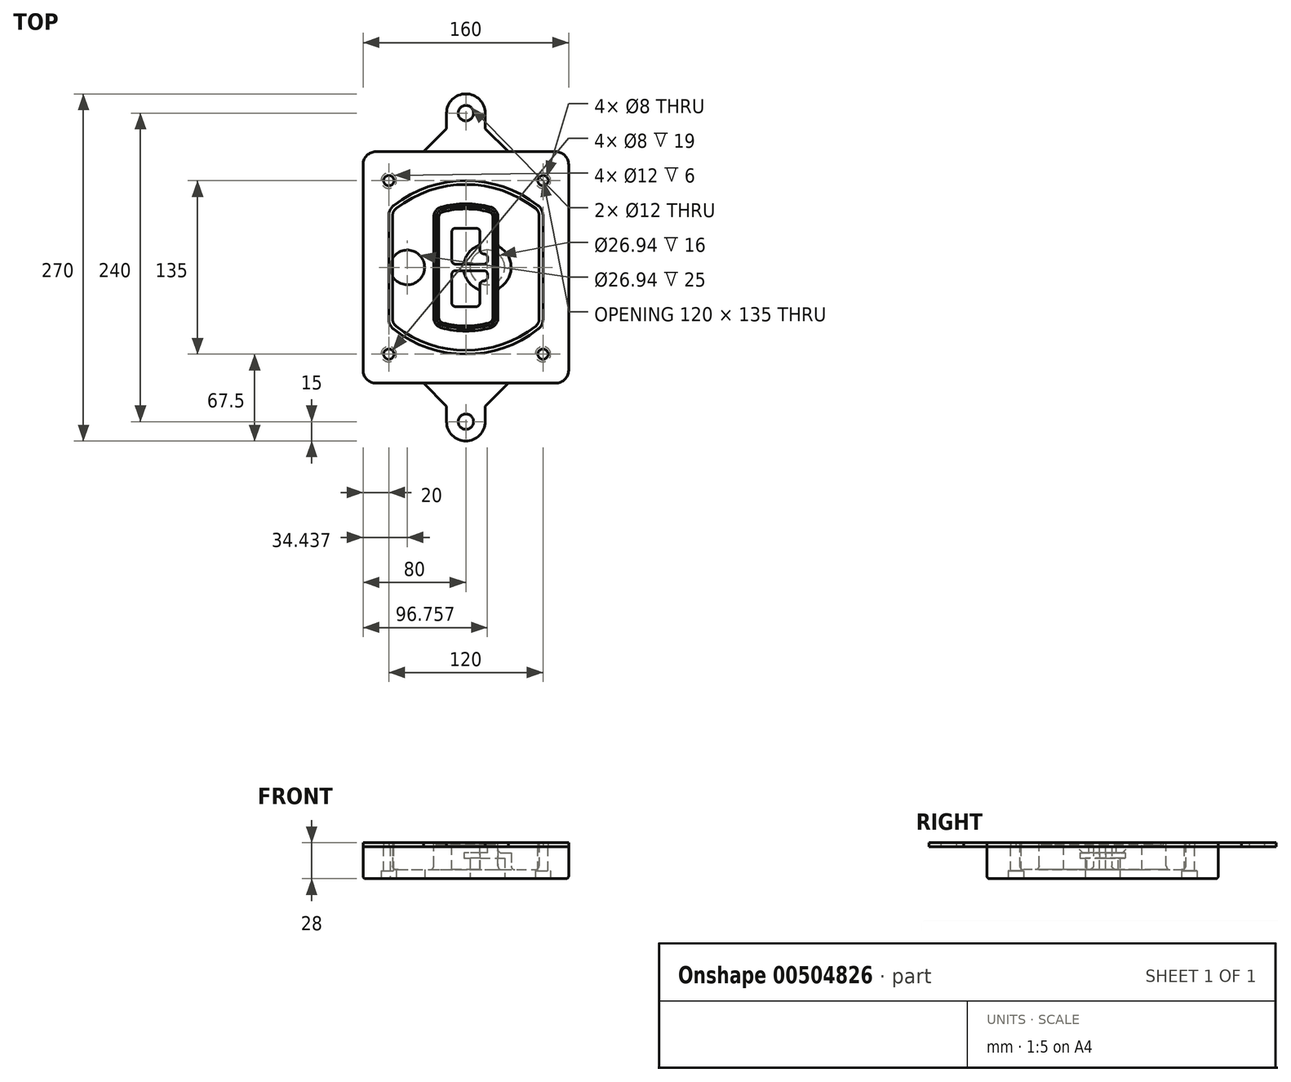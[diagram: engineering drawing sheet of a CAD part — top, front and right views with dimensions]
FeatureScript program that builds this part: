
annotation { "Feature Type Name" : "Feature", "Feature Type Description" : "" }
export const myFeature = defineFeature(function(context is Context, id is Id, definition is map)
    precondition{}
    {
        {
            var Q0;
            Q0=qCreatedBy(makeId("Top.planeOp"),FACE);
            var sketch = newSketch(context, id + "F0", { "sketchPlane" : qUnion([Q0])});
            skPoint(sketch, "E0.rect.middle", {"position": v(0, 0) * mm});
            skLineSegment(sketch, "E1.bottom", {"start": v(-70, -90) * mm, "end": v(70, -90) * mm});
            skLineSegment(sketch, "E1.top", {"start": v(-70, 90) * mm, "end": v(70, 90) * mm});
            skLineSegment(sketch, "E1.left", {"start": v(-80, -80) * mm, "end": v(-80, 80) * mm});
            skLineSegment(sketch, "E1.right", {"start": v(80, -80) * mm, "end": v(80, 80) * mm});
            skLineSegment(sketch, "E2", {"start": v(-80, 90) * mm, "end": v(80, -90) * mm, "construction": true});
            skLineSegment(sketch, "E3", {"start": v(80, 90) * mm, "end": v(-80, -90) * mm, "construction": true});
            skCircle(sketch, "E4", {"center": v(-60, 67.5) * mm, "radius": 4 * mm});
            skCircle(sketch, "E5", {"center": v(60, 67.5) * mm, "radius": 4 * mm});
            skCircle(sketch, "E6", {"center": v(60, -67.5) * mm, "radius": 4 * mm});
            skCircle(sketch, "E7", {"center": v(-60, -67.5) * mm, "radius": 4 * mm});
            skLineSegment(sketch, "E8", {"start": v(-60, 67.5) * mm, "end": v(60, 67.5) * mm, "construction": true});
            skLineSegment(sketch, "E9", {"start": v(60, 67.5) * mm, "end": v(60, -67.5) * mm, "construction": true});
            skLineSegment(sketch, "E10", {"start": v(60, -67.5) * mm, "end": v(-60, -67.5) * mm, "construction": true});
            skLineSegment(sketch, "E11", {"start": v(-60, -67.5) * mm, "end": v(-60, 67.5) * mm, "construction": true});
            skLineSegment(sketch, "E12", {"start": v(-60, 40.3) * mm, "end": v(-60, -40.3) * mm});
            skLineSegment(sketch, "E13", {"start": v(60, 40.3) * mm, "end": v(60, -40.3) * mm});
            skArc(sketch, "E14", {"start": v(56.15, 48.18) * mm, "mid": v(0, 67.5) * mm, "end": v(-56.15, 48.18) * mm});
            skArc(sketch, "E15", {"start": v(-56.15, -48.18) * mm, "mid": v(0, -67.5) * mm, "end": v(56.15, -48.18) * mm});
            skLineSegment(sketch, "E16", {"start": v(-60, 0) * mm, "end": v(60, 0) * mm, "construction": true});
            skPoint(sketch, "E17.visualSharp", {"position": v(-60, -45) * mm});
            skArc(sketch, "E17.filletArc", {"start": v(-60, -40.3) * mm, "mid": v(-58.99, -44.68) * mm, "end": v(-56.15, -48.18) * mm});
            skPoint(sketch, "E18.visualSharp", {"position": v(-60, 45) * mm});
            skArc(sketch, "E18.filletArc", {"start": v(-56.15, 48.18) * mm, "mid": v(-58.99, 44.68) * mm, "end": v(-60, 40.3) * mm});
            skPoint(sketch, "E19.visualSharp", {"position": v(60, 45) * mm});
            skArc(sketch, "E19.filletArc", {"start": v(60, 40.3) * mm, "mid": v(58.99, 44.68) * mm, "end": v(56.15, 48.18) * mm});
            skPoint(sketch, "E20.visualSharp", {"position": v(60, -45) * mm});
            skArc(sketch, "E20.filletArc", {"start": v(56.15, -48.18) * mm, "mid": v(58.99, -44.68) * mm, "end": v(60, -40.3) * mm});
            skPoint(sketch, "E21.visualSharp", {"position": v(-80, 90) * mm});
            skArc(sketch, "E21.filletArc", {"start": v(-70, 90) * mm, "mid": v(-77.07, 87.07) * mm, "end": v(-80, 80) * mm});
            skPoint(sketch, "E22.visualSharp", {"position": v(80, 90) * mm});
            skArc(sketch, "E22.filletArc", {"start": v(80, 80) * mm, "mid": v(77.07, 87.07) * mm, "end": v(70, 90) * mm});
            skPoint(sketch, "E23.visualSharp", {"position": v(80, -90) * mm});
            skArc(sketch, "E23.filletArc", {"start": v(70, -90) * mm, "mid": v(77.07, -87.07) * mm, "end": v(80, -80) * mm});
            skPoint(sketch, "E24.visualSharp", {"position": v(-80, -90) * mm});
            skArc(sketch, "E24.filletArc", {"start": v(-80, -80) * mm, "mid": v(-77.07, -87.07) * mm, "end": v(-70, -90) * mm});
            skArc(sketch, "E25.0", {"start": v(57, 40.3) * mm, "mid": v(56.3, 43.36) * mm, "end": v(54.3, 45.81) * mm});
            skLineSegment(sketch, "E25.1", {"start": v(57, 40.3) * mm, "end": v(57, -40.3) * mm});
            skArc(sketch, "E25.2", {"start": v(54.3, -45.81) * mm, "mid": v(56.3, -43.36) * mm, "end": v(57, -40.3) * mm});
            skArc(sketch, "E25.3", {"start": v(-54.3, -45.81) * mm, "mid": v(0, -64.5) * mm, "end": v(54.3, -45.81) * mm});
            skArc(sketch, "E25.4", {"start": v(-57, -40.3) * mm, "mid": v(-56.3, -43.36) * mm, "end": v(-54.3, -45.81) * mm});
            skArc(sketch, "E25.5", {"start": v(54.3, 45.81) * mm, "mid": v(0, 64.5) * mm, "end": v(-54.3, 45.81) * mm});
            skLineSegment(sketch, "E25.6", {"start": v(-57, 40.3) * mm, "end": v(-57, -40.3) * mm});
            skArc(sketch, "E25.7", {"start": v(-54.3, 45.81) * mm, "mid": v(-56.3, 43.36) * mm, "end": v(-57, 40.3) * mm});
            skArc(sketch, "E26.0", {"start": v(-58.62, 51.33) * mm, "mid": v(-62.58, 46.43) * mm, "end": v(-64, 40.3) * mm});
            skArc(sketch, "E26.1", {"start": v(58.62, 51.33) * mm, "mid": v(0, 71.5) * mm, "end": v(-58.62, 51.33) * mm});
            skArc(sketch, "E26.2", {"start": v(64, 40.3) * mm, "mid": v(62.58, 46.43) * mm, "end": v(58.62, 51.33) * mm});
            skLineSegment(sketch, "E26.3", {"start": v(64, 40.3) * mm, "end": v(64, -40.3) * mm});
            skArc(sketch, "E26.4", {"start": v(58.62, -51.33) * mm, "mid": v(62.58, -46.43) * mm, "end": v(64, -40.3) * mm});
            skLineSegment(sketch, "E26.5", {"start": v(-64, 40.3) * mm, "end": v(-64, -40.3) * mm});
            skArc(sketch, "E26.6", {"start": v(-58.62, -51.33) * mm, "mid": v(0, -71.5) * mm, "end": v(58.62, -51.33) * mm});
            skArc(sketch, "E26.7", {"start": v(-64, -40.3) * mm, "mid": v(-62.58, -46.43) * mm, "end": v(-58.62, -51.33) * mm});
            skSolve(sketch);
        }
        {
            var Q0;
            Q0=makeQuery(id+"F0.imprint","IMPRINT",FACE,{"disambiguationData":[TD([[makeQuery(id+"F0.imprint","IMPRINT",EDGE,{"derivedFrom":sQuery(id+"F0.wireOp",EDGE,"E1.bottom")}),1.0]])]});
            var Q1;
            Q1=makeQuery(id+"F0.imprint","IMPRINT",FACE,{"disambiguationData":[TD([[makeQuery(id+"F0.imprint","IMPRINT",EDGE,{"derivedFrom":sQuery(id+"F0.wireOp",EDGE,"E12")}),1.0]])]});
            var Q2;
            Q2=makeQuery(id+"F0.imprint","IMPRINT",FACE,{"disambiguationData":[TD([[makeQuery(id+"F0.imprint","IMPRINT",EDGE,{"derivedFrom":sQuery(id+"F0.wireOp",EDGE,"E25.0")}),1.0]])]});
            var Q3;
            Q3=makeQuery(id+"F0.imprint","IMPRINT",FACE,{"disambiguationData":[TD([[makeQuery(id+"F0.imprint","IMPRINT",EDGE,{"derivedFrom":sQuery(id+"F0.wireOp",EDGE,"E12")}),-1.0]])]});
            extrude(context, id + "F1", {"entities" : qUnion([Q0, Q1, Q2, Q3]), "oppositeDirection" : true, "depth" : 25 * mm});
        }
        {
            var Q0;
            Q0=makeQuery(id+"F0.imprint","IMPRINT",FACE,{"disambiguationData":[TD([[makeQuery(id+"F0.imprint","IMPRINT",EDGE,{"derivedFrom":sQuery(id+"F0.wireOp",EDGE,"E12")}),1.0]])]});
            extrude(context, id + "F2", {"entities" : qUnion([Q0]), "operationType" : NewBodyOperationType.ADD, "depth" : 3 * mm});
        }
        {
            var Q0;
            Q0=makeQuery(id+"F0.imprint","IMPRINT",FACE,{"disambiguationData":[TD([[makeQuery(id+"F0.imprint","IMPRINT",EDGE,{"derivedFrom":sQuery(id+"F0.wireOp",EDGE,"E25.0")}),1.0]])]});
            extrude(context, id + "F3", {"entities" : qUnion([Q0]), "operationType" : NewBodyOperationType.REMOVE, "oppositeDirection" : true, "depth" : 18 * mm});
        }
        {
            var Q0;
            Q0=makeQuery(id+"F2.opExtrude","CAP_FACE",FACE,{"disambiguationData":[OSD([sQuery(id+"F0.wireOp",EDGE,"E12"),sQuery(id+"F0.wireOp",EDGE,"E13"),sQuery(id+"F0.wireOp",EDGE,"E14"),sQuery(id+"F0.wireOp",EDGE,"E15"),sQuery(id+"F0.wireOp",EDGE,"E17.filletArc"),sQuery(id+"F0.wireOp",EDGE,"E18.filletArc"),sQuery(id+"F0.wireOp",EDGE,"E19.filletArc"),sQuery(id+"F0.wireOp",EDGE,"E20.filletArc"),sQuery(id+"F0.wireOp",EDGE,"E25.0"),sQuery(id+"F0.wireOp",EDGE,"E25.1"),sQuery(id+"F0.wireOp",EDGE,"E25.2"),sQuery(id+"F0.wireOp",EDGE,"E25.3"),sQuery(id+"F0.wireOp",EDGE,"E25.4"),sQuery(id+"F0.wireOp",EDGE,"E25.5"),sQuery(id+"F0.wireOp",EDGE,"E25.6"),sQuery(id+"F0.wireOp",EDGE,"E25.7")])],"isStart":false});
            var sketch = newSketch(context, id + "F4", { "sketchPlane" : qUnion([Q0])});
            skArc(sketch, "E27.0", {"start": v(-19.08, -46.97) * mm, "mid": v(0, -49.5) * mm, "end": v(19.08, -46.97) * mm});
            skArc(sketch, "E28.0", {"start": v(19.08, 46.97) * mm, "mid": v(0, 49.5) * mm, "end": v(-19.08, 46.97) * mm});
            skLineSegment(sketch, "E29", {"start": v(-25, 39.25) * mm, "end": v(-25, -39.25) * mm});
            skLineSegment(sketch, "E30", {"start": v(25, 39.25) * mm, "end": v(25, -39.25) * mm});
            skLineSegment(sketch, "E31", {"start": v(-25, 45.1) * mm, "end": v(25, 45.1) * mm, "construction": true});
            skLineSegment(sketch, "E32", {"start": v(-25, -45.1) * mm, "end": v(25, -45.1) * mm, "construction": true});
            skPoint(sketch, "E33.visualSharp", {"position": v(-25, 45.1) * mm});
            skArc(sketch, "E33.filletArc", {"start": v(-19.08, 46.97) * mm, "mid": v(-23.35, 44.11) * mm, "end": v(-25, 39.25) * mm});
            skPoint(sketch, "E34.visualSharp", {"position": v(25, 45.1) * mm});
            skArc(sketch, "E34.filletArc", {"start": v(25, 39.25) * mm, "mid": v(23.35, 44.11) * mm, "end": v(19.08, 46.97) * mm});
            skPoint(sketch, "E35.visualSharp", {"position": v(25, -45.1) * mm});
            skArc(sketch, "E35.filletArc", {"start": v(19.08, -46.97) * mm, "mid": v(23.35, -44.11) * mm, "end": v(25, -39.25) * mm});
            skPoint(sketch, "E36.visualSharp", {"position": v(-25, -45.1) * mm});
            skArc(sketch, "E36.filletArc", {"start": v(-25, -39.25) * mm, "mid": v(-23.35, -44.11) * mm, "end": v(-19.08, -46.97) * mm});
            skArc(sketch, "E37.0", {"start": v(54.3, 45.81) * mm, "mid": v(0, 64.5) * mm, "end": v(-54.3, 45.81) * mm});
            skArc(sketch, "E37.1", {"start": v(-54.3, 45.81) * mm, "mid": v(-56.3, 43.36) * mm, "end": v(-57, 40.3) * mm});
            skLineSegment(sketch, "E37.2", {"start": v(-57, 40.3) * mm, "end": v(-57, -40.3) * mm});
            skArc(sketch, "E37.3", {"start": v(-57, -40.3) * mm, "mid": v(-56.3, -43.36) * mm, "end": v(-54.3, -45.81) * mm});
            skArc(sketch, "E37.4", {"start": v(-54.3, -45.81) * mm, "mid": v(0, -64.5) * mm, "end": v(54.3, -45.81) * mm});
            skArc(sketch, "E37.5", {"start": v(54.3, -45.81) * mm, "mid": v(56.3, -43.36) * mm, "end": v(57, -40.3) * mm});
            skLineSegment(sketch, "E37.6", {"start": v(57, 40.3) * mm, "end": v(57, -40.3) * mm});
            skArc(sketch, "E37.7", {"start": v(57, 40.3) * mm, "mid": v(56.3, 43.36) * mm, "end": v(54.3, 45.81) * mm});
            skLineSegment(sketch, "E38.0", {"start": v(23, 39.25) * mm, "end": v(23, -39.25) * mm});
            skArc(sketch, "E38.1", {"start": v(18.56, -45.04) * mm, "mid": v(21.76, -42.9) * mm, "end": v(23, -39.25) * mm});
            skArc(sketch, "E38.2", {"start": v(-18.56, -45.04) * mm, "mid": v(0, -47.5) * mm, "end": v(18.56, -45.04) * mm});
            skArc(sketch, "E38.3", {"start": v(-23, -39.25) * mm, "mid": v(-21.76, -42.9) * mm, "end": v(-18.56, -45.04) * mm});
            skLineSegment(sketch, "E38.4", {"start": v(-23, 39.25) * mm, "end": v(-23, -39.25) * mm});
            skArc(sketch, "E38.5", {"start": v(23, 39.25) * mm, "mid": v(21.76, 42.9) * mm, "end": v(18.56, 45.04) * mm});
            skArc(sketch, "E38.6", {"start": v(-18.56, 45.04) * mm, "mid": v(-21.76, 42.9) * mm, "end": v(-23, 39.25) * mm});
            skArc(sketch, "E38.7", {"start": v(18.56, 45.04) * mm, "mid": v(0, 47.5) * mm, "end": v(-18.56, 45.04) * mm});
            skArc(sketch, "E39.0", {"start": v(21, 39.25) * mm, "mid": v(20.18, 41.68) * mm, "end": v(18.04, 43.1) * mm});
            skLineSegment(sketch, "E39.1", {"start": v(21, 39.25) * mm, "end": v(21, -39.25) * mm});
            skArc(sketch, "E39.2", {"start": v(18.04, -43.1) * mm, "mid": v(20.18, -41.68) * mm, "end": v(21, -39.25) * mm});
            skArc(sketch, "E39.3", {"start": v(-18.04, -43.1) * mm, "mid": v(0, -45.5) * mm, "end": v(18.04, -43.1) * mm});
            skArc(sketch, "E39.4", {"start": v(-21, -39.25) * mm, "mid": v(-20.18, -41.68) * mm, "end": v(-18.04, -43.1) * mm});
            skArc(sketch, "E39.5", {"start": v(18.04, 43.1) * mm, "mid": v(0, 45.5) * mm, "end": v(-18.04, 43.1) * mm});
            skLineSegment(sketch, "E39.6", {"start": v(-21, 39.25) * mm, "end": v(-21, -39.25) * mm});
            skArc(sketch, "E39.7", {"start": v(-18.04, 43.1) * mm, "mid": v(-20.18, 41.68) * mm, "end": v(-21, 39.25) * mm});
            skLineSegment(sketch, "E40", {"start": v(-25, 0) * mm, "end": v(25, 0) * mm, "construction": true});
            skLineSegment(sketch, "E41", {"start": v(-11, 5.5) * mm, "end": v(-11, 27.5) * mm});
            skLineSegment(sketch, "E42", {"start": v(-8, 30.5) * mm, "end": v(8, 30.5) * mm});
            skLineSegment(sketch, "E43", {"start": v(11, 27.5) * mm, "end": v(11, 13.5) * mm});
            skLineSegment(sketch, "E44", {"start": v(14, 10.5) * mm, "end": v(14, 10.5) * mm});
            skLineSegment(sketch, "E45", {"start": v(17, 7.5) * mm, "end": v(17, 5.5) * mm});
            skLineSegment(sketch, "E46", {"start": v(14, 2.5) * mm, "end": v(-8, 2.5) * mm});
            skPoint(sketch, "E47.visualSharp", {"position": v(-11, 30.5) * mm});
            skArc(sketch, "E47.filletArc", {"start": v(-8, 30.5) * mm, "mid": v(-10.12, 29.62) * mm, "end": v(-11, 27.5) * mm});
            skPoint(sketch, "E48.visualSharp", {"position": v(11, 30.5) * mm});
            skArc(sketch, "E48.filletArc", {"start": v(11, 27.5) * mm, "mid": v(10.12, 29.62) * mm, "end": v(8, 30.5) * mm});
            skPoint(sketch, "E49.visualSharp", {"position": v(11, 10.5) * mm});
            skArc(sketch, "E49.filletArc", {"start": v(11, 13.5) * mm, "mid": v(11.88, 11.38) * mm, "end": v(14, 10.5) * mm});
            skPoint(sketch, "E50.visualSharp", {"position": v(17, 10.5) * mm});
            skArc(sketch, "E50.filletArc", {"start": v(17, 7.5) * mm, "mid": v(16.12, 9.62) * mm, "end": v(14, 10.5) * mm});
            skPoint(sketch, "E51.visualSharp", {"position": v(17, 2.5) * mm});
            skArc(sketch, "E51.filletArc", {"start": v(14, 2.5) * mm, "mid": v(16.12, 3.38) * mm, "end": v(17, 5.5) * mm});
            skPoint(sketch, "E52.visualSharp", {"position": v(-11, 2.5) * mm});
            skArc(sketch, "E52.filletArc", {"start": v(-11, 5.5) * mm, "mid": v(-10.12, 3.38) * mm, "end": v(-8, 2.5) * mm});
            skLineSegment(sketch, "E53.0.MirrorCS", {"start": v(14, -2.5) * mm, "end": v(-8, -2.5) * mm});
            skArc(sketch, "E54.0.MirrorCS", {"start": v(-11, -5.5) * mm, "mid": v(-10.12, -3.38) * mm, "end": v(-8, -2.5) * mm});
            skLineSegment(sketch, "E55.0.MirrorCS", {"start": v(-11, -5.5) * mm, "end": v(-11, -27.5) * mm});
            skArc(sketch, "E56.0.MirrorCS", {"start": v(-8, -30.5) * mm, "mid": v(-10.12, -29.62) * mm, "end": v(-11, -27.5) * mm});
            skLineSegment(sketch, "E57.0.MirrorCS", {"start": v(-8, -30.5) * mm, "end": v(8, -30.5) * mm});
            skArc(sketch, "E58.0.MirrorCS", {"start": v(11, -27.5) * mm, "mid": v(10.12, -29.62) * mm, "end": v(8, -30.5) * mm});
            skLineSegment(sketch, "E59.0.MirrorCS", {"start": v(11, -27.5) * mm, "end": v(11, -13.5) * mm});
            skArc(sketch, "E60.0.MirrorCS", {"start": v(11, -13.5) * mm, "mid": v(11.88, -11.38) * mm, "end": v(14, -10.5) * mm});
            skArc(sketch, "E61.0.MirrorCS", {"start": v(17, -7.5) * mm, "mid": v(16.12, -9.62) * mm, "end": v(14, -10.5) * mm});
            skLineSegment(sketch, "E62.0.MirrorCS", {"start": v(17, -7.5) * mm, "end": v(17, -5.5) * mm});
            skArc(sketch, "E63.0.MirrorCS", {"start": v(14, -2.5) * mm, "mid": v(16.12, -3.38) * mm, "end": v(17, -5.5) * mm});
            skSolve(sketch);
        }
        {
            var Q0;
            Q0=makeQuery(id+"F4.imprint","IMPRINT",FACE,{"disambiguationData":[TD([[makeQuery(id+"F4.imprint","IMPRINT",EDGE,{"derivedFrom":sQuery(id+"F4.wireOp",EDGE,"E27.0")}),1.0]])]});
            var Q1;
            Q1=makeQuery(id+"F4.imprint","IMPRINT",FACE,{"disambiguationData":[TD([[makeQuery(id+"F4.imprint","IMPRINT",EDGE,{"derivedFrom":sQuery(id+"F4.wireOp",EDGE,"E38.0")}),-1.0]])]});
            var Q2;
            Q2=makeQuery(id+"F4.imprint","IMPRINT",FACE,{"disambiguationData":[TD([[makeQuery(id+"F4.imprint","IMPRINT",EDGE,{"derivedFrom":sQuery(id+"F4.wireOp",EDGE,"E39.0")}),1.0]])]});
            extrude(context, id + "F5", {"entities" : qUnion([Q0, Q1, Q2]), "operationType" : NewBodyOperationType.ADD, "endBound" : BoundingType.UP_TO_NEXT, "oppositeDirection" : true, "depth" : 25 * mm});
        }
        {
            var Q0;
            Q0=makeQuery(id+"F4.imprint","IMPRINT",FACE,{"disambiguationData":[TD([[makeQuery(id+"F4.imprint","IMPRINT",EDGE,{"derivedFrom":sQuery(id+"F4.wireOp",EDGE,"E38.0")}),-1.0]])]});
            extrude(context, id + "F6", {"entities" : qUnion([Q0]), "operationType" : NewBodyOperationType.REMOVE, "oppositeDirection" : true, "depth" : 2 * mm});
        }
        {
            var Q0;
            Q0=makeQuery(id+"F1.opExtrude","CAP_FACE",FACE,{"disambiguationData":[OSD([sQuery(id+"F0.wireOp",EDGE,"E1.bottom"),sQuery(id+"F0.wireOp",EDGE,"E1.top"),sQuery(id+"F0.wireOp",EDGE,"E1.left"),sQuery(id+"F0.wireOp",EDGE,"E1.right"),sQuery(id+"F0.wireOp",EDGE,"E4"),sQuery(id+"F0.wireOp",EDGE,"E5"),sQuery(id+"F0.wireOp",EDGE,"E6"),sQuery(id+"F0.wireOp",EDGE,"E7"),sQuery(id+"F0.wireOp",EDGE,"E21.filletArc"),sQuery(id+"F0.wireOp",EDGE,"E22.filletArc"),sQuery(id+"F0.wireOp",EDGE,"E23.filletArc"),sQuery(id+"F0.wireOp",EDGE,"E24.filletArc")])],"isStart":false});
            var sketch = newSketch(context, id + "F7", { "sketchPlane" : qUnion([Q0])});
            skCircle(sketch, "E64", {"center": v(16.76, 0) * mm, "radius": 13.47 * mm});
            skCircle(sketch, "E65", {"center": v(-45.56, 0) * mm, "radius": 13.47 * mm});
            skLineSegment(sketch, "E66", {"start": v(80, 0) * mm, "end": v(-80, 0) * mm});
            skCircle(sketch, "E67", {"center": v(16.76, 0) * mm, "radius": 18.47 * mm});
            skCircle(sketch, "E68", {"center": v(60, -67.5) * mm, "radius": 6 * mm});
            skCircle(sketch, "E69", {"center": v(-60, -67.5) * mm, "radius": 6 * mm});
            skCircle(sketch, "E70", {"center": v(-60, 67.5) * mm, "radius": 6 * mm});
            skCircle(sketch, "E71", {"center": v(60, 67.5) * mm, "radius": 6 * mm});
            skSolve(sketch);
        }
        {
            var Q0;
            {var subQ1=sQuery(id+"F7.wireOp",EDGE,"E66");var subQ4=sQuery(id+"F7.wireOp",EDGE,"E64");var subQ6=makeQuery(id+"F7.imprint","INTERSECT",VERTEX,{"disambiguationData":[OD(0.0)],"derivedFrom":[subQ4,subQ1]});Q0=makeQuery(id+"F7.imprint","IMPRINT",FACE,{"disambiguationData":[TD([[makeQuery(id+"F7.imprint","IMPRINT",EDGE,{"disambiguationData":[TD([[subQ6,-1.0]])],"derivedFrom":subQ4}),-1.0]])]});}
            var Q1;
            {var subQ0=sQuery(id+"F7.wireOp",EDGE,"E66");var subQ1=sQuery(id+"F7.wireOp",EDGE,"E64");var subQ3=makeQuery(id+"F7.imprint","INTERSECT",VERTEX,{"disambiguationData":[OD(0.0)],"derivedFrom":[subQ1,subQ0]});Q1=makeQuery(id+"F7.imprint","IMPRINT",FACE,{"disambiguationData":[TD([[makeQuery(id+"F7.imprint","IMPRINT",EDGE,{"disambiguationData":[TD([[subQ3,-1.0]])],"derivedFrom":subQ1}),1.0]])]});}
            var Q2;
            {var subQ0=sQuery(id+"F7.wireOp",EDGE,"E66");var subQ1=sQuery(id+"F7.wireOp",EDGE,"E64");var subQ3=makeQuery(id+"F7.imprint","INTERSECT",VERTEX,{"disambiguationData":[OD(0.0)],"derivedFrom":[subQ1,subQ0]});Q2=makeQuery(id+"F7.imprint","IMPRINT",FACE,{"disambiguationData":[TD([[makeQuery(id+"F7.imprint","IMPRINT",EDGE,{"disambiguationData":[TD([[subQ3,1.0]])],"derivedFrom":subQ1}),1.0]])]});}
            var Q3;
            {var subQ1=sQuery(id+"F7.wireOp",EDGE,"E66");var subQ4=sQuery(id+"F7.wireOp",EDGE,"E64");var subQ6=makeQuery(id+"F7.imprint","INTERSECT",VERTEX,{"disambiguationData":[OD(0.0)],"derivedFrom":[subQ4,subQ1]});Q3=makeQuery(id+"F7.imprint","IMPRINT",FACE,{"disambiguationData":[TD([[makeQuery(id+"F7.imprint","IMPRINT",EDGE,{"disambiguationData":[TD([[subQ6,1.0]])],"derivedFrom":subQ4}),-1.0]])]});}
            extrude(context, id + "F8", {"entities" : qUnion([Q0, Q1, Q2, Q3]), "operationType" : NewBodyOperationType.ADD, "oppositeDirection" : true, "depth" : 20 * mm});
        }
        {
            var Q0;
            {var subQ0=sQuery(id+"F7.wireOp",EDGE,"E66");var subQ1=sQuery(id+"F7.wireOp",EDGE,"E64");var subQ3=makeQuery(id+"F7.imprint","INTERSECT",VERTEX,{"disambiguationData":[OD(0.0)],"derivedFrom":[subQ1,subQ0]});Q0=makeQuery(id+"F7.imprint","IMPRINT",FACE,{"disambiguationData":[TD([[makeQuery(id+"F7.imprint","IMPRINT",EDGE,{"disambiguationData":[TD([[subQ3,-1.0]])],"derivedFrom":subQ1}),1.0]])]});}
            var Q1;
            {var subQ0=sQuery(id+"F7.wireOp",EDGE,"E66");var subQ1=sQuery(id+"F7.wireOp",EDGE,"E64");var subQ3=makeQuery(id+"F7.imprint","INTERSECT",VERTEX,{"disambiguationData":[OD(0.0)],"derivedFrom":[subQ1,subQ0]});Q1=makeQuery(id+"F7.imprint","IMPRINT",FACE,{"disambiguationData":[TD([[makeQuery(id+"F7.imprint","IMPRINT",EDGE,{"disambiguationData":[TD([[subQ3,1.0]])],"derivedFrom":subQ1}),1.0]])]});}
            extrude(context, id + "F9", {"entities" : qUnion([Q0, Q1]), "operationType" : NewBodyOperationType.REMOVE, "oppositeDirection" : true, "depth" : 16 * mm});
        }
        {
            var Q0;
            {var subQ0=sQuery(id+"F7.wireOp",EDGE,"E66");var subQ1=sQuery(id+"F7.wireOp",EDGE,"E65");var subQ3=makeQuery(id+"F7.imprint","INTERSECT",VERTEX,{"disambiguationData":[OD(0.0)],"derivedFrom":[subQ1,subQ0]});Q0=makeQuery(id+"F7.imprint","IMPRINT",FACE,{"disambiguationData":[TD([[makeQuery(id+"F7.imprint","IMPRINT",EDGE,{"disambiguationData":[TD([[subQ3,-1.0]])],"derivedFrom":subQ1}),1.0]])]});}
            var Q1;
            {var subQ0=sQuery(id+"F7.wireOp",EDGE,"E66");var subQ1=sQuery(id+"F7.wireOp",EDGE,"E65");var subQ3=makeQuery(id+"F7.imprint","INTERSECT",VERTEX,{"disambiguationData":[OD(0.0)],"derivedFrom":[subQ1,subQ0]});Q1=makeQuery(id+"F7.imprint","IMPRINT",FACE,{"disambiguationData":[TD([[makeQuery(id+"F7.imprint","IMPRINT",EDGE,{"disambiguationData":[TD([[subQ3,1.0]])],"derivedFrom":subQ1}),1.0]])]});}
            extrude(context, id + "F10", {"entities" : qUnion([Q0, Q1]), "operationType" : NewBodyOperationType.REMOVE, "oppositeDirection" : true, "depth" : 25 * mm});
        }
        {
            var Q0;
            Q0=makeQuery(id+"F7.imprint","IMPRINT",FACE,{"disambiguationData":[TD([[makeQuery(id+"F7.imprint","IMPRINT",EDGE,{"derivedFrom":sQuery(id+"F7.wireOp",EDGE,"E68")}),1.0]])]});
            var Q1;
            Q1=makeQuery(id+"F7.imprint","IMPRINT",FACE,{"disambiguationData":[TD([[makeQuery(id+"F7.imprint","IMPRINT",EDGE,{"derivedFrom":makeQuery(id+"F1.opExtrude","CAP_EDGE",EDGE,{"disambiguationData":[OSD([sQuery(id+"F0.wireOp",EDGE,"E5")])],"isStart":false})}),-1.0]])]});
            var Q2;
            Q2=makeQuery(id+"F7.imprint","IMPRINT",FACE,{"disambiguationData":[TD([[makeQuery(id+"F7.imprint","IMPRINT",EDGE,{"derivedFrom":sQuery(id+"F7.wireOp",EDGE,"E69")}),1.0]])]});
            var Q3;
            Q3=makeQuery(id+"F7.imprint","IMPRINT",FACE,{"disambiguationData":[TD([[makeQuery(id+"F7.imprint","IMPRINT",EDGE,{"derivedFrom":makeQuery(id+"F1.opExtrude","CAP_EDGE",EDGE,{"disambiguationData":[OSD([sQuery(id+"F0.wireOp",EDGE,"E4")])],"isStart":false})}),-1.0]])]});
            var Q4;
            Q4=makeQuery(id+"F7.imprint","IMPRINT",FACE,{"disambiguationData":[TD([[makeQuery(id+"F7.imprint","IMPRINT",EDGE,{"derivedFrom":sQuery(id+"F7.wireOp",EDGE,"E70")}),1.0]])]});
            var Q5;
            Q5=makeQuery(id+"F7.imprint","IMPRINT",FACE,{"disambiguationData":[TD([[makeQuery(id+"F7.imprint","IMPRINT",EDGE,{"derivedFrom":makeQuery(id+"F1.opExtrude","CAP_EDGE",EDGE,{"disambiguationData":[OSD([sQuery(id+"F0.wireOp",EDGE,"E7")])],"isStart":false})}),-1.0]])]});
            var Q6;
            Q6=makeQuery(id+"F7.imprint","IMPRINT",FACE,{"disambiguationData":[TD([[makeQuery(id+"F7.imprint","IMPRINT",EDGE,{"derivedFrom":sQuery(id+"F7.wireOp",EDGE,"E71")}),1.0]])]});
            var Q7;
            Q7=makeQuery(id+"F7.imprint","IMPRINT",FACE,{"disambiguationData":[TD([[makeQuery(id+"F7.imprint","IMPRINT",EDGE,{"derivedFrom":makeQuery(id+"F1.opExtrude","CAP_EDGE",EDGE,{"disambiguationData":[OSD([sQuery(id+"F0.wireOp",EDGE,"E6")])],"isStart":false})}),-1.0]])]});
            extrude(context, id + "F11", {"entities" : qUnion([Q0, Q1, Q2, Q3, Q4, Q5, Q6, Q7]), "operationType" : NewBodyOperationType.REMOVE, "oppositeDirection" : true, "depth" : 6 * mm});
        }
        {
            var Q0;
            Q0=makeQuery(id+"F9.boolean.opBoolean","COPY",FACE,{"derivedFrom":makeQuery(id+"F9.opExtrude","CAP_FACE",FACE,{"disambiguationData":[OSD([sQuery(id+"F7.wireOp",EDGE,"E64")])],"isStart":false})});
            var sketch = newSketch(context, id + "F12", { "sketchPlane" : qUnion([Q0])});
            skArc(sketch, "E72.0", {"start": v(11, 17.55) * mm, "mid": v(2.57, 11.82) * mm, "end": v(-1.54, 2.5) * mm});
            skArc(sketch, "E72.1", {"start": v(-1.54, -2.5) * mm, "mid": v(2.57, -11.82) * mm, "end": v(11, -17.55) * mm});
            skLineSegment(sketch, "E73", {"start": v(-1.54, -2.5) * mm, "end": v(14, -2.5) * mm});
            skLineSegment(sketch, "E74.0", {"start": v(14, 2.5) * mm, "end": v(-1.54, 2.5) * mm});
            skArc(sketch, "E74.1", {"start": v(14, 2.5) * mm, "mid": v(16.12, 3.38) * mm, "end": v(17, 5.5) * mm});
            skLineSegment(sketch, "E74.2", {"start": v(17, 7.5) * mm, "end": v(17, 5.5) * mm});
            skArc(sketch, "E74.3", {"start": v(17, 7.5) * mm, "mid": v(16.12, 9.62) * mm, "end": v(14, 10.5) * mm});
            skArc(sketch, "E74.4", {"start": v(11, 13.5) * mm, "mid": v(11.88, 11.38) * mm, "end": v(14, 10.5) * mm});
            skLineSegment(sketch, "E74.5", {"start": v(11, 17.55) * mm, "end": v(11, 13.5) * mm});
            skLineSegment(sketch, "E74.7", {"start": v(14, -2.5) * mm, "end": v(-1.54, -2.5) * mm});
            skArc(sketch, "E74.8", {"start": v(14, -2.5) * mm, "mid": v(16.12, -3.38) * mm, "end": v(17, -5.5) * mm});
            skLineSegment(sketch, "E74.9", {"start": v(17, -7.5) * mm, "end": v(17, -5.5) * mm});
            skArc(sketch, "E74.10", {"start": v(17, -7.5) * mm, "mid": v(16.12, -9.62) * mm, "end": v(14, -10.5) * mm});
            skArc(sketch, "E74.11", {"start": v(11, -13.5) * mm, "mid": v(11.88, -11.38) * mm, "end": v(14, -10.5) * mm});
            skLineSegment(sketch, "E74.12", {"start": v(11, -17.55) * mm, "end": v(11, -13.5) * mm});
            skPoint(sketch, "E75.orphan", {"position": v(11, -27.5) * mm});
            skPoint(sketch, "E76.orphan", {"position": v(-8, -2.5) * mm});
            skPoint(sketch, "E77.orphan", {"position": v(-8, 2.5) * mm});
            skPoint(sketch, "E78.orphan", {"position": v(11, 27.5) * mm});
            skSolve(sketch);
        }
        {
            var Q0;
            {var subQ7=sQuery(id+"F12.wireOp",EDGE,"E72.0");var subQ14=sQuery(id+"F12.wireOp",EDGE,"E72.1");var subQ16=sQuery(id+"F12.wireOp",EDGE,"E74.1");var subQ18=sQuery(id+"F12.wireOp",EDGE,"E74.8");Q0=qUnion([makeQuery(id+"F12.imprint","IMPRINT",FACE,{"disambiguationData":[TD([[makeQuery(id+"F12.imprint","IMPRINT",EDGE,{"derivedFrom":subQ7}),1.0]])]}),makeQuery(id+"F12.imprint","IMPRINT",FACE,{"disambiguationData":[TD([[makeQuery(id+"F12.imprint","IMPRINT",EDGE,{"derivedFrom":subQ14}),1.0]])]}),makeQuery(id+"F12.imprint","IMPRINT",FACE,{"disambiguationData":[TD([[makeQuery(id+"F12.imprint","IMPRINT",EDGE,{"derivedFrom":subQ16}),1.0]])]}),makeQuery(id+"F12.imprint","IMPRINT",FACE,{"disambiguationData":[TD([[makeQuery(id+"F12.imprint","IMPRINT",EDGE,{"derivedFrom":subQ18}),-1.0]])]})]);}
            var Q1;
            Q1=makeQuery(id+"F5.boolean.opBoolean","SPLIT",FACE,{"disambiguationData":[TD([makeQuery(id+"F5.opExtrude","SWEPT_FACE",FACE,{"disambiguationData":[OSD([sQuery(id+"F4.wireOp",EDGE,"E41")])]})])],"derivedFrom":makeQuery(id+"F3.boolean.opBoolean","COPY",FACE,{"derivedFrom":makeQuery(id+"F3.opExtrude","CAP_FACE",FACE,{"disambiguationData":[OSD([sQuery(id+"F0.wireOp",EDGE,"E25.0"),sQuery(id+"F0.wireOp",EDGE,"E25.1"),sQuery(id+"F0.wireOp",EDGE,"E25.2"),sQuery(id+"F0.wireOp",EDGE,"E25.3"),sQuery(id+"F0.wireOp",EDGE,"E25.4"),sQuery(id+"F0.wireOp",EDGE,"E25.5"),sQuery(id+"F0.wireOp",EDGE,"E25.6"),sQuery(id+"F0.wireOp",EDGE,"E25.7")])],"isStart":false})})});
            extrude(context, id + "F13", {"entities" : qUnion([Q0]), "operationType" : NewBodyOperationType.REMOVE, "endBound" : BoundingType.UP_TO_SURFACE, "endBoundEntityFace" : qUnion([Q1]), "depth" : 25 * mm});
        }
        {
            var Q0;
            Q0=makeQuery(id+"F3.boolean.opBoolean","COPY",EDGE,{"derivedFrom":makeQuery(id+"F3.opExtrude","CAP_EDGE",EDGE,{"disambiguationData":[OSD([sQuery(id+"F0.wireOp",EDGE,"E25.6")])],"isStart":false})});
            var Q1;
            Q1=makeQuery(id+"F8.boolean.opBoolean","INTERSECT",EDGE,{"derivedFrom":[makeQuery(id+"F5.opExtrude","SWEPT_FACE",FACE,{"disambiguationData":[OSD([sQuery(id+"F4.wireOp",EDGE,"E30")])]}),makeQuery(id+"F8.opExtrude","CAP_FACE",FACE,{"disambiguationData":[OSD([sQuery(id+"F7.wireOp",EDGE,"E67")])],"isStart":false})]});
            var Q2;
            Q2=makeQuery(id+"F8.boolean.opBoolean","INTERSECT",EDGE,{"disambiguationData":[OD(1.0)],"derivedFrom":[makeQuery(id+"F5.opExtrude","SWEPT_FACE",FACE,{"disambiguationData":[OSD([sQuery(id+"F4.wireOp",EDGE,"E30")])]}),makeQuery(id+"F8.opExtrude","SWEPT_FACE",FACE,{"disambiguationData":[OSD([sQuery(id+"F7.wireOp",EDGE,"E67")])]})]});
            var Q3;
            {var subQ0=sQuery(id+"F4.wireOp",EDGE,"E30");Q3=makeQuery(id+"F8.boolean.opBoolean","SPLIT",EDGE,{"disambiguationData":[TD([makeQuery(id+"F5.opExtrude","SWEPT_FACE",FACE,{"disambiguationData":[OSD([sQuery(id+"F4.wireOp",EDGE,"E35.filletArc")])]})])],"derivedFrom":makeQuery(id+"F5.opExtrude","CAP_EDGE",EDGE,{"disambiguationData":[OSD([subQ0])],"isStart":false})});}
            var Q4;
            {var subQ0=sQuery(id+"F0.wireOp",EDGE,"E25.7");var subQ1=sQuery(id+"F0.wireOp",EDGE,"E25.1");var subQ2=sQuery(id+"F0.wireOp",EDGE,"E25.6");var subQ3=sQuery(id+"F0.wireOp",EDGE,"E25.5");var subQ4=sQuery(id+"F0.wireOp",EDGE,"E25.4");var subQ5=sQuery(id+"F0.wireOp",EDGE,"E25.0");var subQ6=sQuery(id+"F0.wireOp",EDGE,"E25.2");var subQ7=sQuery(id+"F0.wireOp",EDGE,"E25.3");Q4=makeQuery(id+"F8.boolean.opBoolean","INTERSECT",EDGE,{"derivedFrom":[makeQuery(id+"F5.boolean.opBoolean","SPLIT",FACE,{"disambiguationData":[TD([makeQuery(id+"F2.opExtrude","SWEPT_FACE",FACE,{"disambiguationData":[OSD([subQ5])]})])],"derivedFrom":makeQuery(id+"F3.boolean.opBoolean","COPY",FACE,{"derivedFrom":makeQuery(id+"F3.opExtrude","CAP_FACE",FACE,{"disambiguationData":[OSD([subQ5,subQ1,subQ6,subQ7,subQ4,subQ3,subQ2,subQ0])],"isStart":false})})}),makeQuery(id+"F8.opExtrude","SWEPT_FACE",FACE,{"disambiguationData":[OSD([sQuery(id+"F7.wireOp",EDGE,"E67")])]})]});}
            var Q5;
            Q5=makeQuery(id+"F8.boolean.opBoolean","INTERSECT",EDGE,{"disambiguationData":[OD(0.0)],"derivedFrom":[makeQuery(id+"F5.opExtrude","SWEPT_FACE",FACE,{"disambiguationData":[OSD([sQuery(id+"F4.wireOp",EDGE,"E30")])]}),makeQuery(id+"F8.opExtrude","SWEPT_FACE",FACE,{"disambiguationData":[OSD([sQuery(id+"F7.wireOp",EDGE,"E67")])]})]});
            fillet(context, id + "F14", {"entities" : qUnion([Q0, Q1, Q2, Q3, Q4, Q5]), "radius" : 3 * mm, "tangentPropagation" : true, "allowEdgeOverflow" : false});
        }
        {
            var Q0;
            Q0=makeQuery(id+"F1.opExtrude","CAP_EDGE",EDGE,{"disambiguationData":[OSD([sQuery(id+"F0.wireOp",EDGE,"E1.bottom")])],"isStart":false});
            fillet(context, id + "F15", {"entities" : qUnion([Q0]), "radius" : 2 * mm, "tangentPropagation" : true, "allowEdgeOverflow" : false});
        }
        {
            var Q0;
            {var subQ0=sQuery(id+"F0.wireOp",EDGE,"E21.filletArc");var subQ1=sQuery(id+"F0.wireOp",EDGE,"E7");var subQ2=sQuery(id+"F0.wireOp",EDGE,"E6");var subQ3=sQuery(id+"F0.wireOp",EDGE,"E5");var subQ4=sQuery(id+"F0.wireOp",EDGE,"E4");var subQ5=sQuery(id+"F0.wireOp",EDGE,"E22.filletArc");var subQ6=sQuery(id+"F0.wireOp",EDGE,"E1.bottom");var subQ7=sQuery(id+"F0.wireOp",EDGE,"E1.right");var subQ8=sQuery(id+"F0.wireOp",EDGE,"E1.top");var subQ9=sQuery(id+"F0.wireOp",EDGE,"E1.left");var subQ10=sQuery(id+"F0.wireOp",EDGE,"E23.filletArc");var subQ11=sQuery(id+"F0.wireOp",EDGE,"E24.filletArc");Q0=makeQuery(id+"F2.boolean.opBoolean","SPLIT",FACE,{"disambiguationData":[TD([makeQuery(id+"F1.opExtrude","SWEPT_FACE",FACE,{"disambiguationData":[OSD([subQ6])]})])],"derivedFrom":makeQuery(id+"F1.opExtrude","CAP_FACE",FACE,{"disambiguationData":[OSD([subQ6,subQ8,subQ9,subQ7,subQ4,subQ3,subQ2,subQ1,subQ0,subQ5,subQ10,subQ11])],"isStart":true})});}
            var sketch = newSketch(context, id + "F16", { "sketchPlane" : qUnion([Q0])});
            skLineSegment(sketch, "E79", {"start": v(-33, 90) * mm, "end": v(-15, 108) * mm});
            skLineSegment(sketch, "E80", {"start": v(33, 90) * mm, "end": v(15, 108) * mm});
            skLineSegment(sketch, "E81", {"start": v(-15, 108) * mm, "end": v(-15, 120) * mm});
            skLineSegment(sketch, "E82", {"start": v(0, 90) * mm, "end": v(0, 120) * mm, "construction": true});
            skPoint(sketch, "E82.endSnap0", {"position": v(0, 90) * mm});
            skArc(sketch, "E83", {"start": v(15, 120) * mm, "mid": v(0, 135) * mm, "end": v(-15, 120) * mm});
            skCircle(sketch, "E84", {"center": v(0, 120) * mm, "radius": 6 * mm});
            skLineSegment(sketch, "E85", {"start": v(15, 108) * mm, "end": v(15, 120) * mm});
            skLineSegment(sketch, "E86", {"start": v(-80, 0) * mm, "end": v(80, 0) * mm, "construction": true});
            skArc(sketch, "E87.MirrorCS", {"start": v(15, -120) * mm, "mid": v(0, -135) * mm, "end": v(-15, -120) * mm});
            skCircle(sketch, "E88.MirrorC", {"center": v(0, -120) * mm, "radius": 6 * mm});
            skLineSegment(sketch, "E89.MirrorCS", {"start": v(-15, -108) * mm, "end": v(-15, -120) * mm});
            skLineSegment(sketch, "E90.MirrorCS", {"start": v(-33, -90) * mm, "end": v(-15, -108) * mm});
            skLineSegment(sketch, "E91.MirrorCS", {"start": v(33, -90) * mm, "end": v(15, -108) * mm});
            skPoint(sketch, "E92.MirrorP", {"position": v(0, -90) * mm});
            skLineSegment(sketch, "E93.MirrorCS", {"start": v(15, -108) * mm, "end": v(15, -120) * mm});
            skLineSegment(sketch, "E94.MirrorCS", {"start": v(0, -90) * mm, "end": v(0, -120) * mm, "construction": true});
            skSolve(sketch);
        }
        {
            var Q0;
            {var subQ0=sQuery(id+"F0.wireOp",EDGE,"E21.filletArc");var subQ1=sQuery(id+"F0.wireOp",EDGE,"E7");var subQ2=sQuery(id+"F0.wireOp",EDGE,"E6");var subQ3=sQuery(id+"F0.wireOp",EDGE,"E5");var subQ4=sQuery(id+"F0.wireOp",EDGE,"E4");var subQ5=sQuery(id+"F0.wireOp",EDGE,"E22.filletArc");var subQ6=sQuery(id+"F0.wireOp",EDGE,"E1.bottom");var subQ7=sQuery(id+"F0.wireOp",EDGE,"E1.right");var subQ8=sQuery(id+"F0.wireOp",EDGE,"E1.top");var subQ9=sQuery(id+"F0.wireOp",EDGE,"E1.left");var subQ10=sQuery(id+"F0.wireOp",EDGE,"E23.filletArc");var subQ11=sQuery(id+"F0.wireOp",EDGE,"E24.filletArc");Q0=makeQuery(id+"F2.boolean.opBoolean","SPLIT",FACE,{"disambiguationData":[TD([makeQuery(id+"F1.opExtrude","SWEPT_FACE",FACE,{"disambiguationData":[OSD([subQ6])]})])],"derivedFrom":makeQuery(id+"F1.opExtrude","CAP_FACE",FACE,{"disambiguationData":[OSD([subQ6,subQ8,subQ9,subQ7,subQ4,subQ3,subQ2,subQ1,subQ0,subQ5,subQ10,subQ11])],"isStart":true})});}
            var Q1;
            {var subQ0=sQuery(id+"F16.wireOp",EDGE,"E79");Q1=makeQuery(id+"F16.imprint","IMPRINT",FACE,{"disambiguationData":[TD([[makeQuery(id+"F16.imprint","IMPRINT",EDGE,{"derivedFrom":subQ0}),-1.0]])]});}
            var Q2;
            {var subQ1=sQuery(id+"F16.wireOp",EDGE,"E91.MirrorCS");Q2=makeQuery(id+"F16.imprint","IMPRINT",FACE,{"disambiguationData":[TD([[makeQuery(id+"F16.imprint","IMPRINT",EDGE,{"derivedFrom":subQ1}),-1.0]])]});}
            var Q3;
            Q3=makeQuery(id+"F2.opExtrude","CAP_FACE",FACE,{"disambiguationData":[OSD([sQuery(id+"F0.wireOp",EDGE,"E12"),sQuery(id+"F0.wireOp",EDGE,"E13"),sQuery(id+"F0.wireOp",EDGE,"E14"),sQuery(id+"F0.wireOp",EDGE,"E15"),sQuery(id+"F0.wireOp",EDGE,"E17.filletArc"),sQuery(id+"F0.wireOp",EDGE,"E18.filletArc"),sQuery(id+"F0.wireOp",EDGE,"E19.filletArc"),sQuery(id+"F0.wireOp",EDGE,"E20.filletArc"),sQuery(id+"F0.wireOp",EDGE,"E25.0"),sQuery(id+"F0.wireOp",EDGE,"E25.1"),sQuery(id+"F0.wireOp",EDGE,"E25.2"),sQuery(id+"F0.wireOp",EDGE,"E25.3"),sQuery(id+"F0.wireOp",EDGE,"E25.4"),sQuery(id+"F0.wireOp",EDGE,"E25.5"),sQuery(id+"F0.wireOp",EDGE,"E25.6"),sQuery(id+"F0.wireOp",EDGE,"E25.7")])],"isStart":false});
            extrude(context, id + "F17", {"entities" : qUnion([Q0, Q1, Q2]), "endBound" : BoundingType.UP_TO_SURFACE, "endBoundEntityFace" : qUnion([Q3]), "depth" : 25 * mm});
        }
    });
